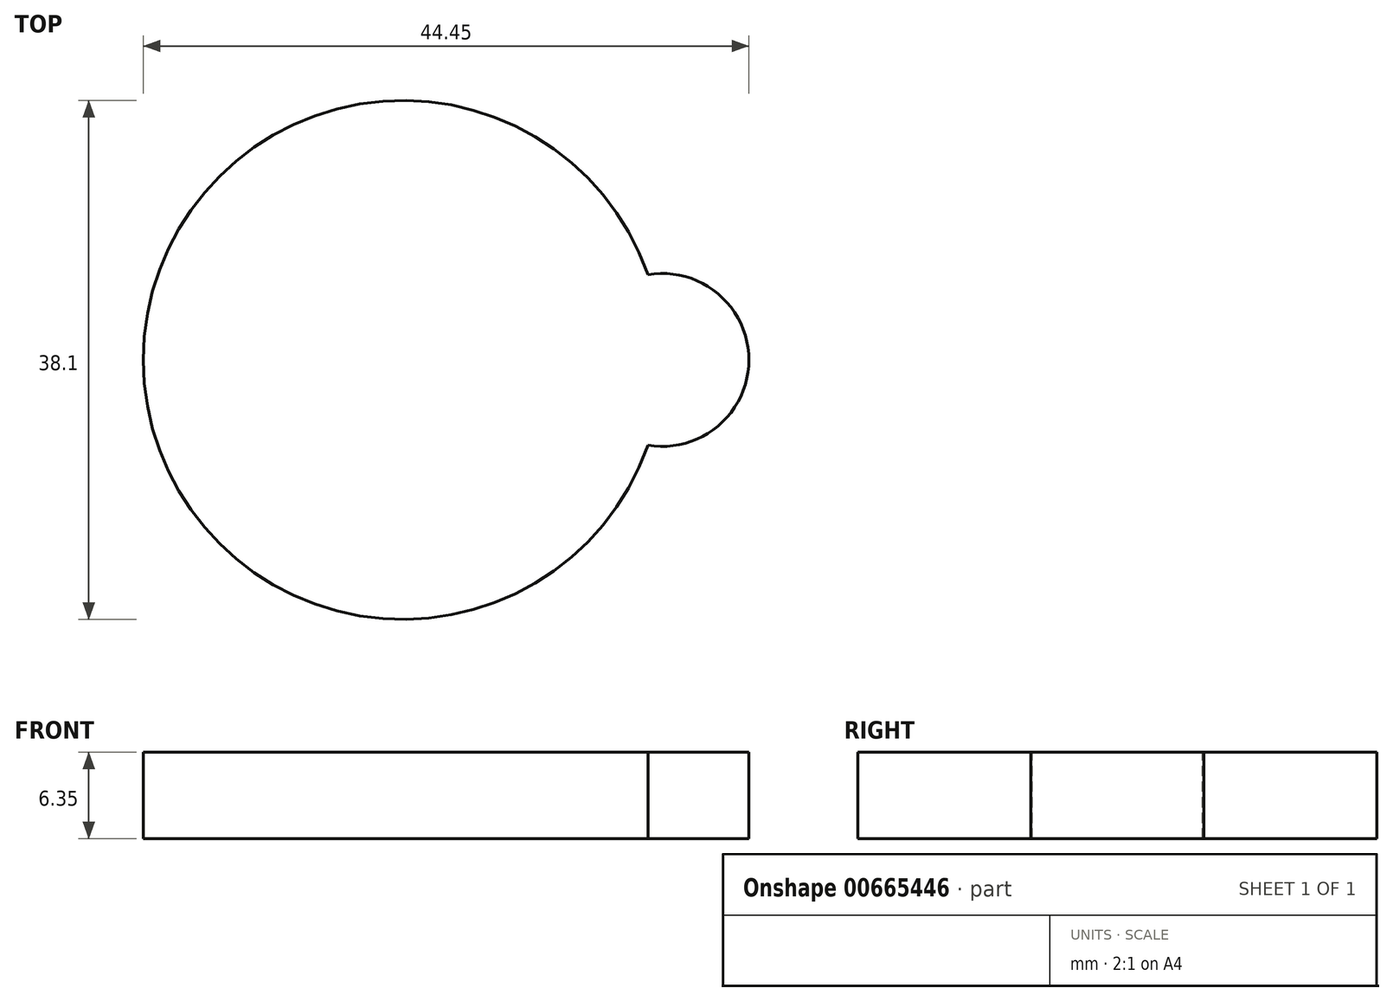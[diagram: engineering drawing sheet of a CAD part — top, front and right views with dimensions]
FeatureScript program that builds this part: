
annotation { "Feature Type Name" : "Feature", "Feature Type Description" : "" }
export const myFeature = defineFeature(function(context is Context, id is Id, definition is map)
    precondition{}
    {
        {
            var Q0;
            Q0=qCreatedBy(makeId("Top.planeOp"),FACE);
            var sketch = newSketch(context, id + "F0", { "sketchPlane" : qUnion([Q0])});
            skCircle(sketch, "E0", {"center": v(0, 0) * mm, "radius": 19.05 * mm});
            skArc(sketch, "E1", {"start": v(18, 6.26) * mm, "mid": v(25.4, 0) * mm, "end": v(18, -6.26) * mm});
            skSolve(sketch);
        }
        {
            var Q0;
            Q0 = qSketchRegion(id + "F0", true);
            extrude(context, id + "F1", {"entities" : qUnion([Q0]), "oppositeDirection" : true, "depth" : 6.35 * mm, "offsetDistance" : 25.4 * mm});
        }
    });
